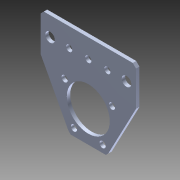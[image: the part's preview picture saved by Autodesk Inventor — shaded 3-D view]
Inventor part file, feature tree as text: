
AUTODESK INVENTOR PART (.ipt)
format: ipt  version: 2015 SP1 (Build 190203100, 203)  size: 140,800 bytes
history: native  units: in
note: dims shown in document units (in); Inventor stores cm internally (conversion verified against a paired STEP export)
features: other x2, extrude x1, imported_body x1, sketch x1
ambient origin geometry x8: Origin, YZ Plane, XZ Plane, XY Plane, X Axis, Y Axis, Z Axis, Center Point
bodies: Body1 (feature_tree)
feature tree (5):
  other  "Cut-Extrude1"
  other  "Bearing Side Gusset1"
  extrude  "Extrusion1"  Depth=1.0in
  imported_body  "Base1"
  sketch  "Sketch1"  dims[d0=0.25in d1=0.25in d2=1.0in d3=0.0in]
